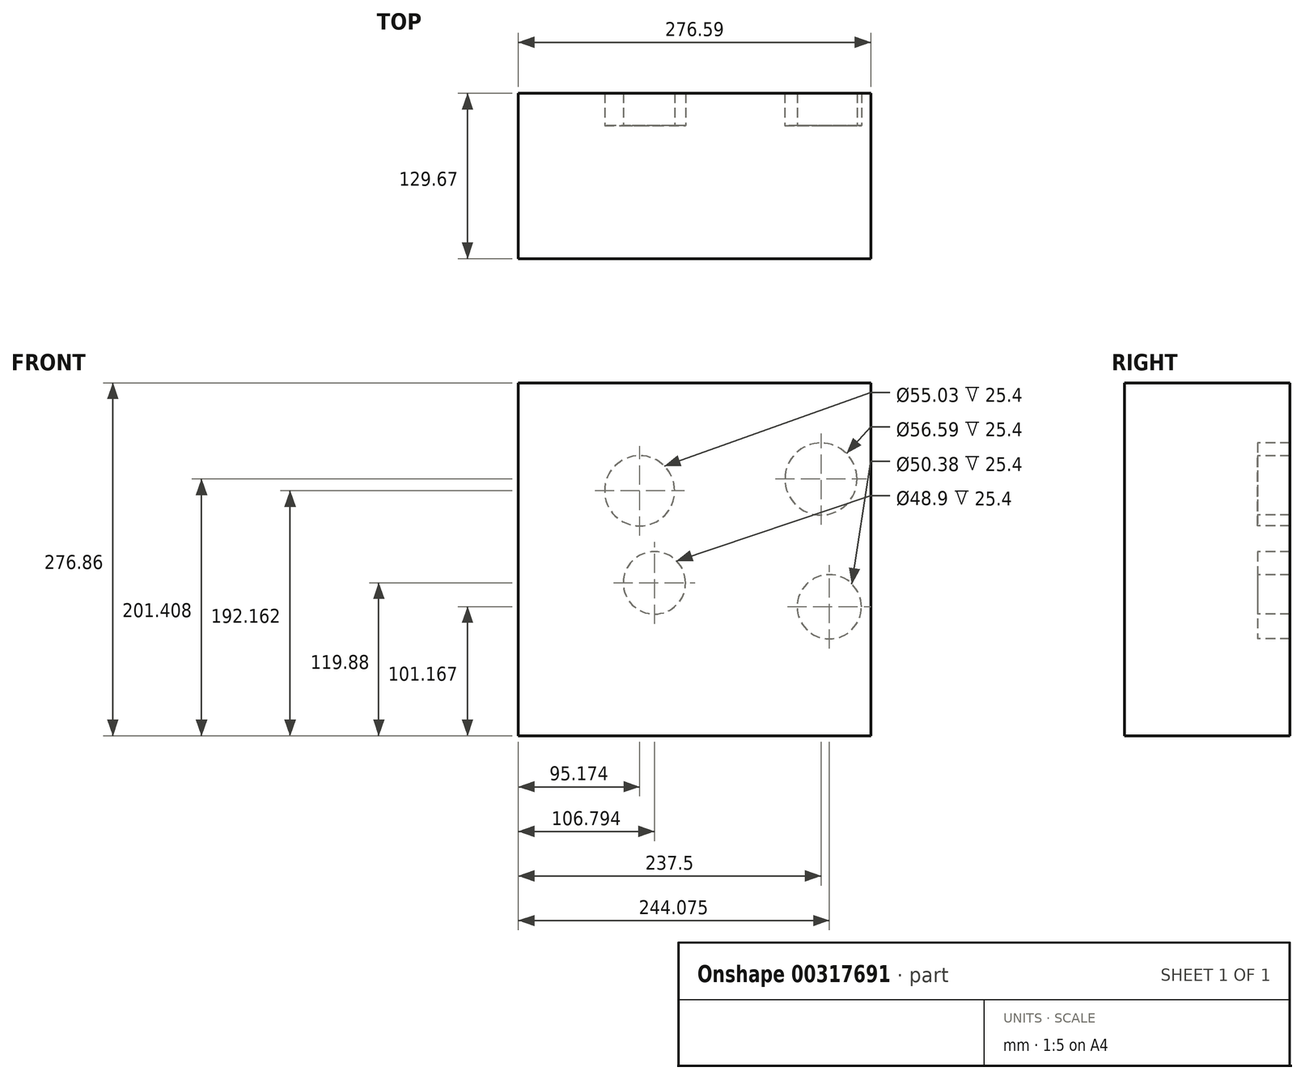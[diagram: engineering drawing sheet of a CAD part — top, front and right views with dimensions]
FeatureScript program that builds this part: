
annotation { "Feature Type Name" : "Feature", "Feature Type Description" : "" }
export const myFeature = defineFeature(function(context is Context, id is Id, definition is map)
    precondition{}
    {
        {
            var Q0;
            Q0=qCreatedBy(makeId("Top.planeOp"),FACE);
            var sketch = newSketch(context, id + "F0", { "sketchPlane" : qUnion([Q0])});
            skLineSegment(sketch, "E0.bottom", {"start": v(-74, -31.08) * mm, "end": v(70.52, -31.08) * mm});
            skLineSegment(sketch, "E0.top", {"start": v(-74, 73.19) * mm, "end": v(70.52, 73.19) * mm});
            skLineSegment(sketch, "E0.left", {"start": v(-74, -31.08) * mm, "end": v(-74, 73.19) * mm});
            skLineSegment(sketch, "E0.right", {"start": v(70.52, -31.08) * mm, "end": v(70.52, 73.19) * mm});
            skSolve(sketch);
        }
        {
            var Q0;
            Q0 = qSketchRegion(id + "F0", true);
            extrude(context, id + "F1", {"entities" : qUnion([Q0]), "depth" : 104.4 * mm});
        }
        {
            var Q0;
            Q0=makeQuery(id+"F1.opExtrude","CAP_FACE",FACE,{"disambiguationData":[OSD([sQuery(id+"F0.wireOp",EDGE,"E0.bottom"),sQuery(id+"F0.wireOp",EDGE,"E0.top"),sQuery(id+"F0.wireOp",EDGE,"E0.left"),sQuery(id+"F0.wireOp",EDGE,"E0.right")])],"isStart":false});
            extrude(context, id + "F2", {"entities" : qUnion([Q0]), "operationType" : NewBodyOperationType.ADD, "oppositeDirection" : true, "depth" : 276.86 * mm});
        }
        {
            var Q0;
            {var subQ0=sQuery(id+"F0.wireOp",EDGE,"E0.right");Q0=makeQuery(id+"F2.boolean.opBoolean","MERGE",FACE,{"derivedFrom":[makeQuery(id+"F1.opExtrude","SWEPT_FACE",FACE,{"disambiguationData":[OSD([subQ0])]}),makeQuery(id+"F2.opExtrude","SWEPT_FACE",FACE,{"disambiguationData":[OSD([subQ0])]})]});}
            extrude(context, id + "F3", {"entities" : qUnion([Q0]), "operationType" : NewBodyOperationType.ADD, "depth" : 132.08 * mm});
        }
        {
            var Q0;
            {var subQ0=sQuery(id+"F0.wireOp",EDGE,"E0.top");Q0=makeQuery(id+"F3.boolean.opBoolean","MERGE",FACE,{"derivedFrom":[makeQuery(id+"F2.boolean.opBoolean","MERGE",FACE,{"derivedFrom":[makeQuery(id+"F1.opExtrude","SWEPT_FACE",FACE,{"disambiguationData":[OSD([subQ0])]}),makeQuery(id+"F2.opExtrude","SWEPT_FACE",FACE,{"disambiguationData":[OSD([subQ0])]})]}),makeQuery(id+"F3.opExtrude","SWEPT_FACE",FACE,{"disambiguationData":[OSD([subQ0,sQuery(id+"F0.wireOp",EDGE,"E0.right")])]})]});}
            var sketch = newSketch(context, id + "F4", { "sketchPlane" : qUnion([Q0])});
            skCircle(sketch, "E1", {"center": v(-32.8, -52.59) * mm, "radius": 24.45 * mm});
            skCircle(sketch, "E2", {"center": v(-170.08, -71.3) * mm, "radius": 25.19 * mm});
            skCircle(sketch, "E3", {"center": v(-163.5, 28.94) * mm, "radius": 28.3 * mm});
            skCircle(sketch, "E4", {"center": v(-21.18, 19.7) * mm, "radius": 27.52 * mm});
            skSolve(sketch);
        }
        {
            var Q0;
            Q0=makeQuery(id+"F4.imprint","IMPRINT",FACE,{"disambiguationData":[TD([[makeQuery(id+"F4.imprint","IMPRINT",EDGE,{"derivedFrom":sQuery(id+"F4.wireOp",EDGE,"E1")}),-1.0]])]});
            extrude(context, id + "F5", {"entities" : qUnion([Q0]), "operationType" : NewBodyOperationType.ADD, "depth" : 25.4 * mm});
        }
    });
